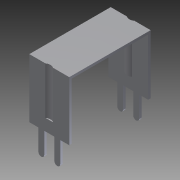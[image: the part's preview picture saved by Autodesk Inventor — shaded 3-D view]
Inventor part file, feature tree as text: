
AUTODESK INVENTOR PART (.ipt)
format: ipt  version: 2011 SP1 (Build 150282100, 282)  size: 118,272 bytes
history: native  units: in
note: dims shown in document units (in); Inventor stores cm internally (conversion verified against a paired STEP export)
features: other x7, extrude x6, sketch x6
ambient origin geometry x8: Origin, YZ Plane, XZ Plane, XY Plane, X Axis, Y Axis, Z Axis, Center Point
bodies: Solid1 (feature_tree)
feature tree (19):
  extrude  "Extrusion1"  Depth=0.642in TaperAngle=0.0deg
  extrude  "Extrusion2"  Depth=0.372in TaperAngle=0.0deg
  extrude  "Extrusion3"  Depth=0.372in TaperAngle=0.0deg
  extrude  "Extrusion4"  [1 undecoded]
  extrude  "Extrusion5"  [1 undecoded]
  extrude  "Extrusion6"  [1 undecoded]
  other  "bracket_to_switch_XY"
  other  "bracket_to_switch_YZ"
  other  "bracket_to_switch_ZX"
  other  "bracket_to_switch_X"
  other  "bracket_to_switch_Y"
  other  "bracket_to_switch_Z"
  other  "bracket_to_switch_Center"
  sketch  "Sketch_1"  dims[d0=0.315in d1=0.0in d2=0.642in d3=0.0in]
  sketch  "Sketch_2"  dims[d4=0.372in d5=0.0in d6=0.372in d7=0.0in]
  sketch  "Sketch_3"  dims[d8=0.372in d9=0.0in d10=0.372in d11=0.0in]
  sketch  "Sketch_4"
  sketch  "Sketch_5"
  sketch  "Sketch_6"
note: 3 required parameter values undecoded (feature->parameter linkage not recoverable at this tier; creation-order binding heuristic only, values carry confidence <= 0.55)
